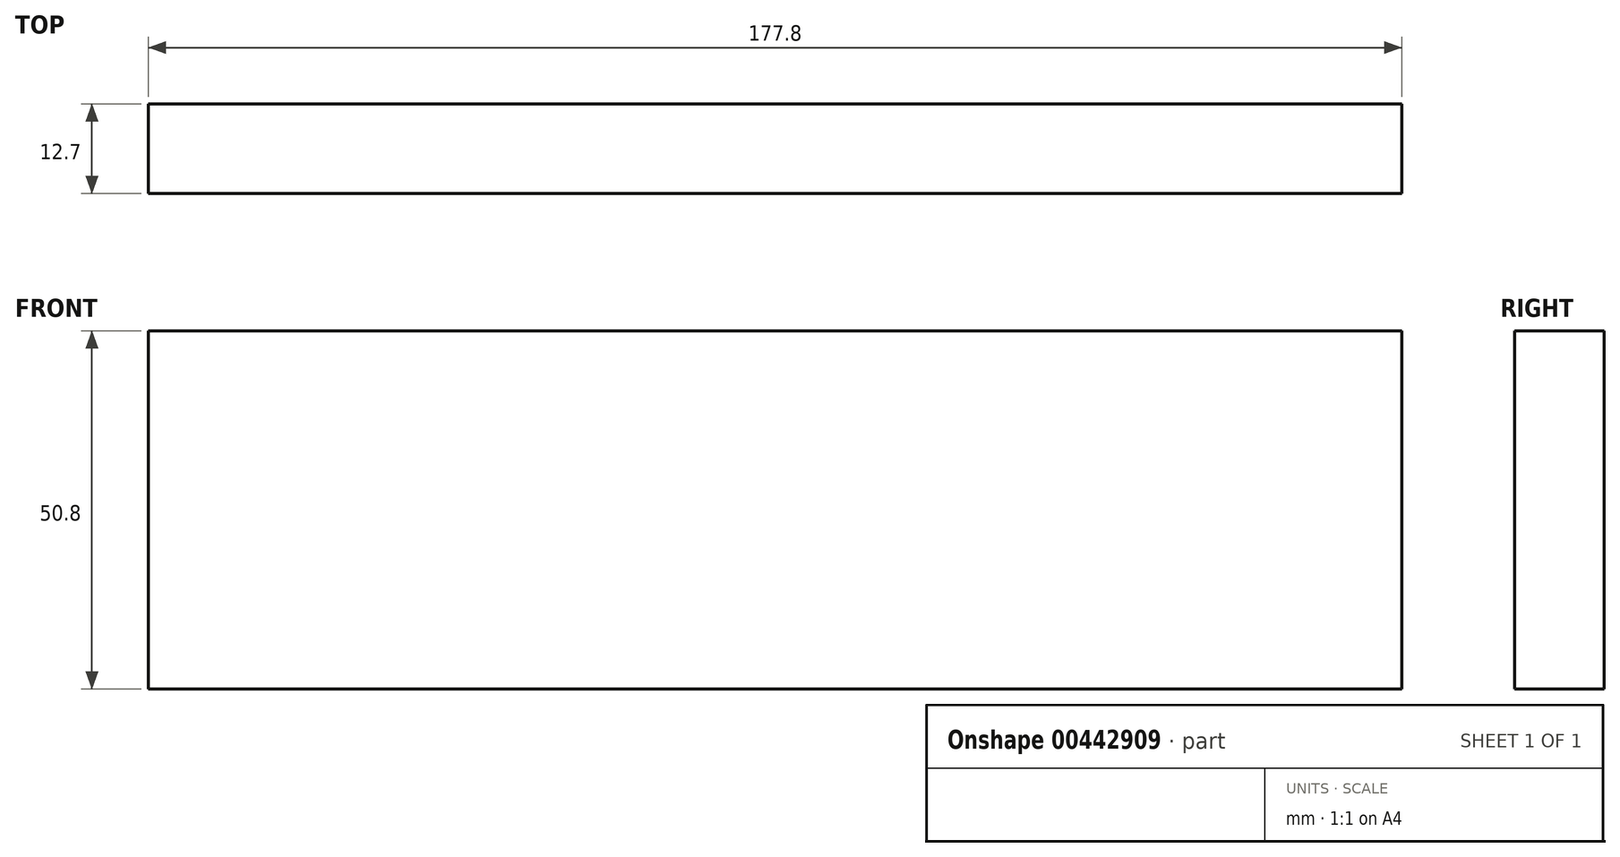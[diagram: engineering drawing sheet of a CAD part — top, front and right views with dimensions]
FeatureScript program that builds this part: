
annotation { "Feature Type Name" : "Feature", "Feature Type Description" : "" }
export const myFeature = defineFeature(function(context is Context, id is Id, definition is map)
    precondition{}
    {
        {
            var Q0;
            Q0=qCreatedBy(makeId("Front.planeOp"),FACE);
            var sketch = newSketch(context, id + "F0", { "sketchPlane" : qUnion([Q0])});
            skLineSegment(sketch, "E0.bottom", {"start": v(-136.48, -10.6) * mm, "end": v(41.32, -10.6) * mm});
            skLineSegment(sketch, "E0.top", {"start": v(-136.48, -61.4) * mm, "end": v(41.32, -61.4) * mm});
            skLineSegment(sketch, "E0.left", {"start": v(-136.48, -10.6) * mm, "end": v(-136.48, -61.4) * mm});
            skLineSegment(sketch, "E0.right", {"start": v(41.32, -10.6) * mm, "end": v(41.32, -61.4) * mm});
            skSolve(sketch);
        }
        {
            var Q0;
            Q0 = qSketchRegion(id + "F0", true);
            extrude(context, id + "F1", {"entities" : qUnion([Q0]), "depth" : 12.7 * mm});
        }
    });
